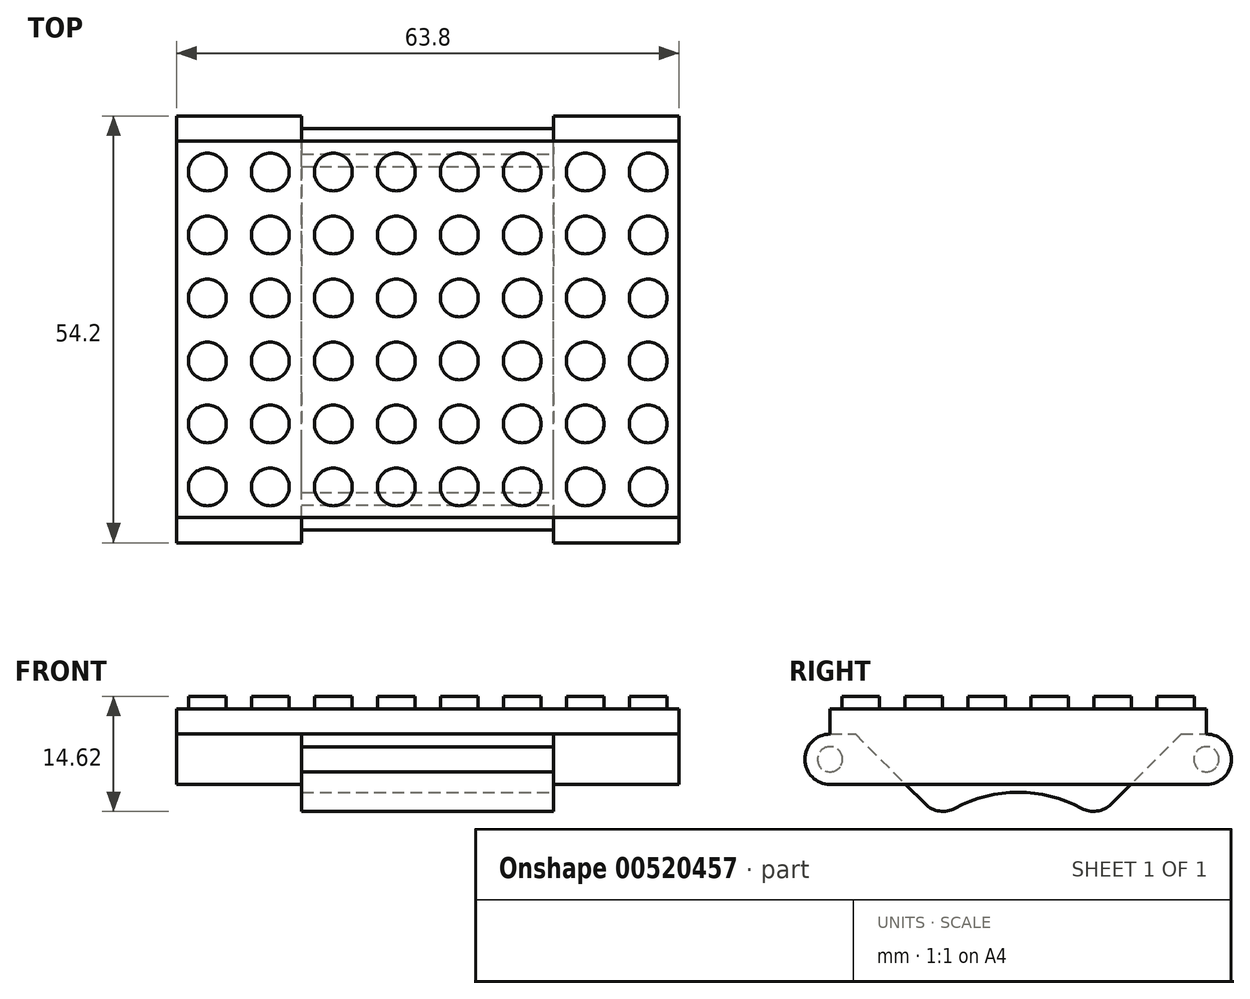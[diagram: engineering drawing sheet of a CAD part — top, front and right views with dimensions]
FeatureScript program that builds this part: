
annotation { "Feature Type Name" : "Feature", "Feature Type Description" : "" }
export const myFeature = defineFeature(function(context is Context, id is Id, definition is map)
    precondition{}
    {
        {
            var Q0;
            Q0=qCreatedBy(makeId("Top.planeOp"),FACE);
            var sketch = newSketch(context, id + "F0", { "sketchPlane" : qUnion([Q0])});
            skLineSegment(sketch, "E0.bottom", {"start": v(31.9, 23.9) * mm, "end": v(-31.9, 23.9) * mm});
            skLineSegment(sketch, "E0.top", {"start": v(31.9, -23.9) * mm, "end": v(-31.9, -23.9) * mm});
            skLineSegment(sketch, "E0.left", {"start": v(31.9, 23.9) * mm, "end": v(31.9, -23.9) * mm});
            skLineSegment(sketch, "E0.right", {"start": v(-31.9, 23.9) * mm, "end": v(-31.9, -23.9) * mm});
            skSolve(sketch);
        }
        {
            var Q0;
            Q0 = qSketchRegion(id + "F0", true);
            extrude(context, id + "F1", {"entities" : qUnion([Q0]), "depth" : 3.2 * mm, "offsetDistance" : 25 * mm});
        }
        {
            var Q0;
            Q0=makeQuery(id+"F1.opExtrude","CAP_FACE",FACE,{"disambiguationData":[OSD([sQuery(id+"F0.wireOp",EDGE,"E0.bottom"),sQuery(id+"F0.wireOp",EDGE,"E0.top"),sQuery(id+"F0.wireOp",EDGE,"E0.left"),sQuery(id+"F0.wireOp",EDGE,"E0.right")])],"isStart":false});
            var sketch = newSketch(context, id + "F2", { "sketchPlane" : qUnion([Q0])});
            skPoint(sketch, "E1.middle", {"position": v(41, 16.58) * mm});
            skCircle(sketch, "E2", {"center": v(-28, 20) * mm, "radius": 2.4 * mm});
            skCircle(sketch, "E3.0.1.0", {"center": v(-28, 12) * mm, "radius": 2.4 * mm});
            skCircle(sketch, "E3.0.2.0", {"center": v(-28, 4) * mm, "radius": 2.4 * mm});
            skCircle(sketch, "E3.0.3.0", {"center": v(-28, -4) * mm, "radius": 2.4 * mm});
            skCircle(sketch, "E3.0.4.0", {"center": v(-28, -12) * mm, "radius": 2.4 * mm});
            skCircle(sketch, "E3.0.5.0", {"center": v(-28, -20) * mm, "radius": 2.4 * mm});
            skCircle(sketch, "E3.1.0.0", {"center": v(-20, 20) * mm, "radius": 2.4 * mm});
            skCircle(sketch, "E3.1.1.0", {"center": v(-20, 12) * mm, "radius": 2.4 * mm});
            skCircle(sketch, "E3.1.2.0", {"center": v(-20, 4) * mm, "radius": 2.4 * mm});
            skCircle(sketch, "E3.1.3.0", {"center": v(-20, -4) * mm, "radius": 2.4 * mm});
            skCircle(sketch, "E3.1.4.0", {"center": v(-20, -12) * mm, "radius": 2.4 * mm});
            skCircle(sketch, "E3.1.5.0", {"center": v(-20, -20) * mm, "radius": 2.4 * mm});
            skCircle(sketch, "E3.2.0.0", {"center": v(-12, 20) * mm, "radius": 2.4 * mm});
            skCircle(sketch, "E3.2.1.0", {"center": v(-12, 12) * mm, "radius": 2.4 * mm});
            skCircle(sketch, "E3.2.2.0", {"center": v(-12, 4) * mm, "radius": 2.4 * mm});
            skCircle(sketch, "E3.2.3.0", {"center": v(-12, -4) * mm, "radius": 2.4 * mm});
            skCircle(sketch, "E3.2.4.0", {"center": v(-12, -12) * mm, "radius": 2.4 * mm});
            skCircle(sketch, "E3.2.5.0", {"center": v(-12, -20) * mm, "radius": 2.4 * mm});
            skCircle(sketch, "E3.3.0.0", {"center": v(-4, 20) * mm, "radius": 2.4 * mm});
            skCircle(sketch, "E3.3.1.0", {"center": v(-4, 12) * mm, "radius": 2.4 * mm});
            skCircle(sketch, "E3.3.2.0", {"center": v(-4, 4) * mm, "radius": 2.4 * mm});
            skCircle(sketch, "E3.3.3.0", {"center": v(-4, -4) * mm, "radius": 2.4 * mm});
            skCircle(sketch, "E3.3.4.0", {"center": v(-4, -12) * mm, "radius": 2.4 * mm});
            skCircle(sketch, "E3.3.5.0", {"center": v(-4, -20) * mm, "radius": 2.4 * mm});
            skCircle(sketch, "E3.4.0.0", {"center": v(4, 20) * mm, "radius": 2.4 * mm});
            skCircle(sketch, "E3.4.1.0", {"center": v(4, 12) * mm, "radius": 2.4 * mm});
            skCircle(sketch, "E3.4.2.0", {"center": v(4, 4) * mm, "radius": 2.4 * mm});
            skCircle(sketch, "E3.4.3.0", {"center": v(4, -4) * mm, "radius": 2.4 * mm});
            skCircle(sketch, "E3.4.4.0", {"center": v(4, -12) * mm, "radius": 2.4 * mm});
            skCircle(sketch, "E3.4.5.0", {"center": v(4, -20) * mm, "radius": 2.4 * mm});
            skCircle(sketch, "E3.5.0.0", {"center": v(12, 20) * mm, "radius": 2.4 * mm});
            skCircle(sketch, "E3.5.1.0", {"center": v(12, 12) * mm, "radius": 2.4 * mm});
            skCircle(sketch, "E3.5.2.0", {"center": v(12, 4) * mm, "radius": 2.4 * mm});
            skCircle(sketch, "E3.5.3.0", {"center": v(12, -4) * mm, "radius": 2.4 * mm});
            skCircle(sketch, "E3.5.4.0", {"center": v(12, -12) * mm, "radius": 2.4 * mm});
            skCircle(sketch, "E3.5.5.0", {"center": v(12, -20) * mm, "radius": 2.4 * mm});
            skCircle(sketch, "E3.6.0.0", {"center": v(20, 20) * mm, "radius": 2.4 * mm});
            skCircle(sketch, "E3.6.1.0", {"center": v(20, 12) * mm, "radius": 2.4 * mm});
            skCircle(sketch, "E3.6.2.0", {"center": v(20, 4) * mm, "radius": 2.4 * mm});
            skCircle(sketch, "E3.6.3.0", {"center": v(20, -4) * mm, "radius": 2.4 * mm});
            skCircle(sketch, "E3.6.4.0", {"center": v(20, -12) * mm, "radius": 2.4 * mm});
            skCircle(sketch, "E3.6.5.0", {"center": v(20, -20) * mm, "radius": 2.4 * mm});
            skCircle(sketch, "E3.7.0.0", {"center": v(28, 20) * mm, "radius": 2.4 * mm});
            skCircle(sketch, "E3.7.1.0", {"center": v(28, 12) * mm, "radius": 2.4 * mm});
            skCircle(sketch, "E3.7.2.0", {"center": v(28, 4) * mm, "radius": 2.4 * mm});
            skCircle(sketch, "E3.7.3.0", {"center": v(28, -4) * mm, "radius": 2.4 * mm});
            skCircle(sketch, "E3.7.4.0", {"center": v(28, -12) * mm, "radius": 2.4 * mm});
            skCircle(sketch, "E3.7.5.0", {"center": v(28, -20) * mm, "radius": 2.4 * mm});
            skLineSegment(sketch, "E3.direction1", {"start": v(-28, 20) * mm, "end": v(-20, 20) * mm, "construction": true});
            skLineSegment(sketch, "E3.direction2", {"start": v(-28, 20) * mm, "end": v(-28, 12) * mm, "construction": true});
            skSolve(sketch);
        }
        {
            var Q0;
            Q0 = qSketchRegion(id + "F2", true);
            extrude(context, id + "F3", {"entities" : qUnion([Q0]), "operationType" : NewBodyOperationType.ADD, "depth" : 1.6 * mm, "offsetDistance" : 25 * mm});
        }
        {
            var Q0;
            Q0=makeQuery(id+"F1.opExtrude","SWEPT_FACE",FACE,{"disambiguationData":[OSD([sQuery(id+"F0.wireOp",EDGE,"E0.left")])]});
            cPlane(context, id + "F4", {"entities" : qUnion([Q0]), "cplaneType" : CPlaneType.OFFSET, "offset" : 15.9 * mm, "oppositeDirection" : true, "width" : 150 * mm, "height" : 150 * mm});
        }
        {
            var Q0;
            Q0=makeQuery(id+"F1.opExtrude","SWEPT_FACE",FACE,{"disambiguationData":[OSD([sQuery(id+"F0.wireOp",EDGE,"E0.left")])]});
            var sketch = newSketch(context, id + "F5", { "sketchPlane" : qUnion([Q0])});
            skLineSegment(sketch, "E4.bottom", {"start": v(23.9, 0) * mm, "end": v(-23.9, 0) * mm});
            skLineSegment(sketch, "E4.top", {"start": v(23.9, -6.4) * mm, "end": v(-23.9, -6.4) * mm});
            skLineSegment(sketch, "E4.left", {"start": v(27.1, -3.2) * mm, "end": v(27.1, -3.2) * mm});
            skLineSegment(sketch, "E4.right", {"start": v(-27.1, -3.2) * mm, "end": v(-27.1, -3.2) * mm});
            skPoint(sketch, "E4.middle", {"position": v(0, -3.2) * mm});
            skPoint(sketch, "E5.visualSharp", {"position": v(-27.1, 0) * mm});
            skArc(sketch, "E5.filletArc", {"start": v(-23.9, 0) * mm, "mid": v(-26.16, -0.94) * mm, "end": v(-27.1, -3.2) * mm});
            skPoint(sketch, "E6.visualSharp", {"position": v(-27.1, -6.4) * mm});
            skArc(sketch, "E6.filletArc", {"start": v(-27.1, -3.2) * mm, "mid": v(-26.16, -5.46) * mm, "end": v(-23.9, -6.4) * mm});
            skPoint(sketch, "E7.visualSharp", {"position": v(27.1, 0) * mm});
            skArc(sketch, "E7.filletArc", {"start": v(27.1, -3.2) * mm, "mid": v(26.16, -0.94) * mm, "end": v(23.9, 0) * mm});
            skPoint(sketch, "E8.visualSharp", {"position": v(27.1, -6.4) * mm});
            skArc(sketch, "E8.filletArc", {"start": v(23.9, -6.4) * mm, "mid": v(26.16, -5.46) * mm, "end": v(27.1, -3.2) * mm});
            skSolve(sketch);
        }
        {
            var Q0;
            Q0 = qSketchRegion(id + "F5", true);
            var Q1;
            Q1=qCreatedBy(id+"F4.planeOp",FACE);
            extrude(context, id + "F6", {"entities" : qUnion([Q0]), "endBound" : BoundingType.UP_TO_SURFACE, "oppositeDirection" : true, "depth" : 25 * mm, "endBoundEntityFace" : qUnion([Q1]), "offsetDistance" : 25 * mm});
        }
        {
            var Q0;
            Q0=makeQuery(id+"F6.opExtrude","SWEPT_BODY",BODY,{"disambiguationData":[OSD([sQuery(id+"F5.wireOp",EDGE,"E4.bottom"),sQuery(id+"F5.wireOp",EDGE,"E4.top"),sQuery(id+"F5.wireOp",EDGE,"E5.filletArc"),sQuery(id+"F5.wireOp",EDGE,"E6.filletArc"),sQuery(id+"F5.wireOp",EDGE,"E7.filletArc"),sQuery(id+"F5.wireOp",EDGE,"E8.filletArc")])]});
            var Q1;
            Q1=qCreatedBy(makeId("Right.planeOp"),FACE);
            mirror(context, id + "F7", {"operationType" : NewBodyOperationType.ADD, "entities" : qUnion([Q0]), "mirrorPlane" : qUnion([Q1])});
        }
        {
            var Q0;
            Q0=makeQuery(id+"F6.opExtrude","CAP_FACE",FACE,{"disambiguationData":[OSD([sQuery(id+"F5.wireOp",EDGE,"E4.bottom"),sQuery(id+"F5.wireOp",EDGE,"E4.top"),sQuery(id+"F5.wireOp",EDGE,"E5.filletArc"),sQuery(id+"F5.wireOp",EDGE,"E6.filletArc"),sQuery(id+"F5.wireOp",EDGE,"E7.filletArc"),sQuery(id+"F5.wireOp",EDGE,"E8.filletArc")])],"isStart":false});
            var sketch = newSketch(context, id + "F8", { "sketchPlane" : qUnion([Q0])});
            skArc(sketch, "E9.0.0", {"start": v(-23.9, 0) * mm, "mid": v(-27.1, -3.2) * mm, "end": v(-23.9, -6.4) * mm, "construction": true});
            skLineSegment(sketch, "E9.0.1", {"start": v(-23.9, -6.4) * mm, "end": v(23.9, -6.4) * mm, "construction": true});
            skArc(sketch, "E9.0.2", {"start": v(23.9, -6.4) * mm, "mid": v(27.1, -3.2) * mm, "end": v(23.9, 0) * mm, "construction": true});
            skLineSegment(sketch, "E9.0.3", {"start": v(23.9, 0) * mm, "end": v(-23.9, 0) * mm, "construction": true});
            skCircle(sketch, "E10", {"center": v(-23.9, -3.2) * mm, "radius": 1.6 * mm});
            skCircle(sketch, "E11", {"center": v(23.9, -3.2) * mm, "radius": 1.6 * mm});
            skLineSegment(sketch, "E12", {"start": v(0, 0) * mm, "end": v(0, -24.25) * mm, "construction": true});
            skPoint(sketch, "E12.endSnap0", {"position": v(0, -6.4) * mm});
            skLineSegment(sketch, "E13", {"start": v(-20.7, 0) * mm, "end": v(-11.82, -8.88) * mm});
            skLineSegment(sketch, "E14.MirrorCS", {"start": v(20.7, 0) * mm, "end": v(11.82, -8.88) * mm});
            skArc(sketch, "E15", {"start": v(-8.03, -9.44) * mm, "mid": v(0, -7.4) * mm, "end": v(8.03, -9.44) * mm});
            skPoint(sketch, "E16.visualSharp", {"position": v(-10, -10.7) * mm});
            skArc(sketch, "E16.filletArc", {"start": v(-11.82, -8.88) * mm, "mid": v(-10.01, -9.79) * mm, "end": v(-8.03, -9.44) * mm});
            skPoint(sketch, "E17.visualSharp", {"position": v(10, -10.7) * mm});
            skArc(sketch, "E17.filletArc", {"start": v(8.03, -9.44) * mm, "mid": v(10.01, -9.79) * mm, "end": v(11.82, -8.88) * mm});
            skLineSegment(sketch, "E18", {"start": v(-20.7, 0) * mm, "end": v(20.7, 0) * mm});
            skSolve(sketch);
        }
        {
            var Q0;
            Q0 = qSketchRegion(id + "F8", true);
            var Q1;
            Q1=makeQuery(id+"F7.opPattern","COPY",FACE,{"derivedFrom":makeQuery(id+"F6.opExtrude","CAP_FACE",FACE,{"disambiguationData":[OSD([sQuery(id+"F5.wireOp",EDGE,"E4.bottom"),sQuery(id+"F5.wireOp",EDGE,"E4.top"),sQuery(id+"F5.wireOp",EDGE,"E5.filletArc"),sQuery(id+"F5.wireOp",EDGE,"E6.filletArc"),sQuery(id+"F5.wireOp",EDGE,"E7.filletArc"),sQuery(id+"F5.wireOp",EDGE,"E8.filletArc")])],"isStart":false}),"instanceName":"1"});
            extrude(context, id + "F9", {"entities" : qUnion([Q0]), "operationType" : NewBodyOperationType.ADD, "endBound" : BoundingType.UP_TO_SURFACE, "depth" : 25 * mm, "endBoundEntityFace" : qUnion([Q1]), "offsetDistance" : 25 * mm});
        }
    });
